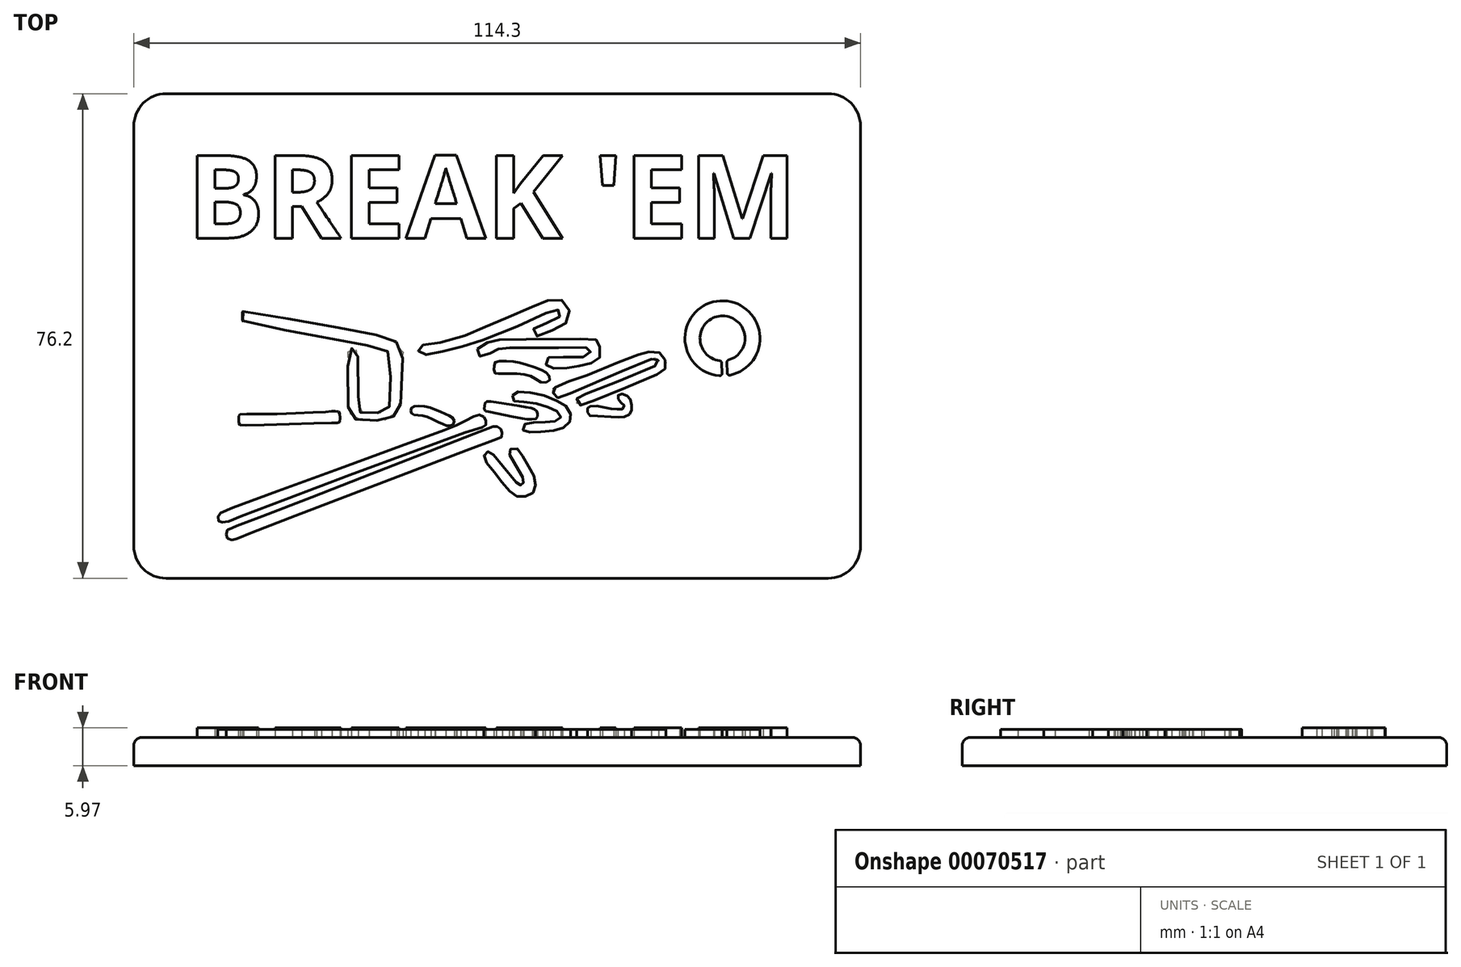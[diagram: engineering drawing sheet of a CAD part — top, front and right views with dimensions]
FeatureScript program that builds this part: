
annotation { "Feature Type Name" : "Feature", "Feature Type Description" : "" }
export const myFeature = defineFeature(function(context is Context, id is Id, definition is map)
    precondition{}
    {
        {
            var Q0;
            Q0=qCreatedBy(makeId("Top.planeOp"),FACE);
            var sketch = newSketch(context, id + "F0", { "sketchPlane" : qUnion([Q0])});
            skLineSegment(sketch, "E0.rect.bottom", {"start": v(57.15, -38.1) * mm, "end": v(-57.15, -38.1) * mm});
            skLineSegment(sketch, "E0.rect.top", {"start": v(57.15, 38.1) * mm, "end": v(-57.15, 38.1) * mm});
            skLineSegment(sketch, "E0.rect.left", {"start": v(57.15, -38.1) * mm, "end": v(57.15, 38.1) * mm});
            skLineSegment(sketch, "E0.rect.right", {"start": v(-57.15, -38.1) * mm, "end": v(-57.15, 38.1) * mm});
            skPoint(sketch, "E0.rect.middle", {"position": v(0, 0) * mm});
            skSolve(sketch);
        }
        {
            var Q0;
            Q0=makeQuery(id+"F0.imprint","IMPRINT",FACE,{"disambiguationData":[TD([[makeQuery(id+"F0.imprint","IMPRINT",EDGE,{"derivedFrom":sQuery(id+"F0.wireOp",EDGE,"E0.rect.bottom")}),-1.0]])]});
            extrude(context, id + "F1", {"entities" : qUnion([Q0]), "depth" : 4.44 * mm});
        }
        {
            var Q0;
            Q0=makeQuery(id+"F1.opExtrude","SWEPT_EDGE",EDGE,{"disambiguationData":[OSD([sQuery(id+"F0.wireOp",EDGE,"E0.rect.bottom"),sQuery(id+"F0.wireOp",EDGE,"E0.rect.right")])]});
            var Q1;
            Q1=makeQuery(id+"F1.opExtrude","SWEPT_EDGE",EDGE,{"disambiguationData":[OSD([sQuery(id+"F0.wireOp",EDGE,"E0.rect.bottom"),sQuery(id+"F0.wireOp",EDGE,"E0.rect.left")])]});
            var Q2;
            Q2=makeQuery(id+"F1.opExtrude","SWEPT_EDGE",EDGE,{"disambiguationData":[OSD([sQuery(id+"F0.wireOp",EDGE,"E0.rect.top"),sQuery(id+"F0.wireOp",EDGE,"E0.rect.left")])]});
            var Q3;
            Q3=makeQuery(id+"F1.opExtrude","SWEPT_EDGE",EDGE,{"disambiguationData":[OSD([sQuery(id+"F0.wireOp",EDGE,"E0.rect.top"),sQuery(id+"F0.wireOp",EDGE,"E0.rect.right")])]});
            fillet(context, id + "F2", {"entities" : qUnion([Q0, Q1, Q2, Q3]), "radius" : 5.08 * mm, "tangentPropagation" : true, "allowEdgeOverflow" : false});
        }
        {
            var Q0;
            Q0=makeQuery(id+"F1.opExtrude","CAP_FACE",FACE,{"disambiguationData":[OSD([sQuery(id+"F0.wireOp",EDGE,"E0.rect.bottom"),sQuery(id+"F0.wireOp",EDGE,"E0.rect.top"),sQuery(id+"F0.wireOp",EDGE,"E0.rect.left"),sQuery(id+"F0.wireOp",EDGE,"E0.rect.right")])],"isStart":false});
            var sketch = newSketch(context, id + "F3", { "sketchPlane" : qUnion([Q0])});
            skFitSpline(sketch, "E1", {"points": [v(-39.94, 3.87) * mm, v(-33.53, 2.82) * mm, v(-25.08, 1.33) * mm, v(-19.72, 0.36) * mm, v(-17.93, -0.18) * mm, v(-16.53, -0.66) * mm, v(-15.41, -1.2) * mm, v(-14.9, -2.03) * mm, v(-14.83, -3.42) * mm, v(-15.17, -10.42) * mm, v(-15.45, -11.43) * mm, v(-15.7, -11.97) * mm, v(-16.18, -12.48) * mm, v(-16.68, -12.87) * mm, v(-17.47, -13.16) * mm, v(-18.32, -13.24) * mm, v(-21.28, -13.3) * mm, v(-21.78, -13.26) * mm, v(-22.24, -13.1) * mm, v(-22.71, -12.74) * mm, v(-23.2, -12.06) * mm, v(-23.4, -11.35) * mm, v(-23.45, -10.11) * mm, v(-23.49, -2.72) * mm, v(-23.36, -2.2) * mm, v(-23.16, -2) * mm, v(-22.9, -1.92) * mm, v(-22.58, -1.92) * mm, v(-22.22, -2.08) * mm, v(-22, -2.47) * mm, v(-21.88, -3.16) * mm, v(-21.87, -3.78) * mm, v(-21.86, -10.73) * mm, v(-21.86, -11.38) * mm, v(-21.83, -11.74) * mm, v(-21.67, -11.92) * mm, v(-21.4, -12.02) * mm, v(-20.92, -12.08) * mm, v(-19.89, -12.1) * mm, v(-18.2, -11.99) * mm, v(-17.61, -11.82) * mm, v(-17.24, -11.5) * mm, v(-17.03, -11.24) * mm, v(-16.87, -10.9) * mm, v(-16.82, -10.46) * mm, v(-16.73, -4.34) * mm, v(-16.76, -2.95) * mm, v(-17.52, -2.23) * mm, v(-19.01, -1.77) * mm, v(-20.47, -1.44) * mm, v(-39.51, 2.08) * mm, v(-39.86, 2.2) * mm, v(-40.02, 2.41) * mm, v(-40.07, 2.7) * mm, v(-40.08, 3.14) * mm, v(-40.07, 3.59) * mm, v(-40.08, 3.74) * mm, v(-39.94, 3.87) * mm]});
            skFitSpline(sketch, "E2", {"points": [v(-40.45, -12.34) * mm, v(-35.1, -12.26) * mm, v(-26.4, -11.88) * mm, v(-25.87, -11.83) * mm, v(-25.43, -11.81) * mm, v(-24.97, -11.87) * mm, v(-24.79, -12) * mm, v(-24.73, -12.4) * mm, v(-24.7, -13.25) * mm, v(-24.82, -13.57) * mm, v(-25.04, -13.64) * mm, v(-25.77, -13.64) * mm, v(-40.22, -14.04) * mm, v(-40.46, -13.97) * mm, v(-40.63, -13.75) * mm, v(-40.68, -13.43) * mm, v(-40.66, -12.95) * mm, v(-40.63, -12.57) * mm, v(-40.55, -12.4) * mm, v(-40.45, -12.34) * mm]});
            skFitSpline(sketch, "E3", {"points": [v(-11.7, -1.39) * mm, v(-10.41, -1.25) * mm, v(-8.79, -1) * mm, v(-5.92, -0.22) * mm, v(-2.9, 1) * mm, v(-1.54, 1.55) * mm, v(0.23, 2.29) * mm, v(3.91, 3.93) * mm, v(6.4, 4.95) * mm, v(7.52, 5.42) * mm, v(8.38, 5.68) * mm, v(9.24, 5.82) * mm, v(10.27, 5.62) * mm, v(10.95, 4.99) * mm, v(11.28, 4.27) * mm, v(11.46, 3.38) * mm, v(11.28, 2.5) * mm, v(10.57, 1.83) * mm, v(9.66, 1.32) * mm, v(8.5, 0.82) * mm, v(7.2, 0.26) * mm, v(6.24, -0.02) * mm, v(5.74, 0) * mm, v(5.58, 0.23) * mm, v(5.63, 1) * mm, v(6.3, 1.44) * mm, v(7.15, 1.79) * mm, v(8.1, 2.16) * mm, v(8.97, 2.54) * mm, v(9.92, 3.1) * mm, v(10.12, 3.62) * mm, v(10.07, 3.83) * mm, v(9.91, 4.02) * mm, v(9.43, 4.14) * mm, v(8.77, 4.06) * mm, v(7.9, 3.72) * mm, v(6.85, 3.2) * mm, v(-0.6, -0.07) * mm, v(-3.24, -0.93) * mm, v(-5.46, -1.67) * mm, v(-7.64, -2.23) * mm, v(-8.97, -2.53) * mm, v(-10.44, -2.83) * mm, v(-11.46, -2.96) * mm, v(-12.11, -2.9) * mm, v(-12.34, -2.72) * mm, v(-12.4, -2.39) * mm, v(-12.43, -2) * mm, v(-12.32, -1.66) * mm, v(-12.1, -1.5) * mm, v(-11.7, -1.39) * mm]});
            skFitSpline(sketch, "E4", {"points": [v(-3.13, -2.04) * mm, v(-2.66, -1.65) * mm, v(-1.66, -1.1) * mm, v(-0.8, -0.79) * mm, v(0.3, -0.58) * mm, v(1.42, -0.53) * mm, v(14.73, -0.43) * mm, v(15.24, -0.5) * mm, v(15.63, -0.63) * mm, v(15.95, -0.88) * mm, v(16.1, -1.27) * mm, v(16.16, -1.63) * mm, v(16.2, -2.68) * mm, v(16.16, -3.25) * mm, v(15.87, -3.69) * mm, v(15.3, -4.03) * mm, v(14.5, -4.36) * mm, v(13.53, -4.62) * mm, v(12.66, -4.77) * mm, v(11.78, -4.9) * mm, v(10.65, -5.05) * mm, v(9.4, -5.1) * mm, v(8.65, -5.1) * mm, v(8.08, -4.9) * mm, v(7.76, -4.64) * mm, v(7.6, -4.22) * mm, v(7.63, -3.73) * mm, v(7.95, -3.45) * mm, v(8.6, -3.35) * mm, v(10.44, -3.34) * mm, v(13.22, -3.31) * mm, v(13.96, -3.18) * mm, v(14.46, -2.92) * mm, v(14.7, -2.46) * mm, v(14.65, -2.02) * mm, v(14.45, -1.84) * mm, v(14, -1.79) * mm, v(13.2, -1.81) * mm, v(1.34, -1.84) * mm, v(0.86, -1.89) * mm, v(0.41, -2) * mm, v(-0.26, -2.3) * mm, v(-0.72, -2.53) * mm, v(-1.17, -2.79) * mm, v(-1.77, -3.16) * mm, v(-2.62, -3.22) * mm, v(-3.01, -2.92) * mm, v(-3.3, -2.45) * mm, v(-3.13, -2.04) * mm]});
            skFitSpline(sketch, "E5", {"points": [v(-0.47, -4.68) * mm, v(-0.44, -4.33) * mm, v(-0.3, -4.09) * mm, v(0.14, -3.97) * mm, v(1.12, -3.94) * mm, v(2.13, -3.99) * mm, v(3.21, -4.1) * mm, v(4.14, -4.35) * mm, v(5.42, -4.75) * mm, v(6.85, -5.3) * mm, v(7.44, -5.6) * mm, v(7.9, -5.93) * mm, v(8.2, -6.34) * mm, v(8.3, -6.7) * mm, v(8.14, -7.1) * mm, v(7.78, -7.29) * mm, v(7.16, -7.35) * mm, v(6.43, -7.02) * mm, v(5.75, -6.56) * mm, v(5.17, -6.26) * mm, v(4.16, -6) * mm, v(3, -5.93) * mm, v(1.95, -5.91) * mm, v(1.07, -5.91) * mm, v(0.44, -5.91) * mm, v(-0.12, -5.94) * mm, v(-0.3, -5.86) * mm, v(-0.4, -5.7) * mm, v(-0.48, -5.4) * mm, v(-0.48, -5.03) * mm, v(-0.47, -4.68) * mm]});
            skFitSpline(sketch, "E6", {"points": [v(9.15, -8.1) * mm, v(10.14, -7.66) * mm, v(11.72, -6.97) * mm, v(13.8, -6.3) * mm, v(19.96, -3.76) * mm, v(22.12, -2.93) * mm, v(23, -2.66) * mm, v(23.67, -2.49) * mm, v(24.41, -2.43) * mm, v(25.1, -2.49) * mm, v(25.63, -2.67) * mm, v(26.1, -3.11) * mm, v(26.34, -3.53) * mm, v(26.5, -4.03) * mm, v(26.54, -4.53) * mm, v(26.44, -5.03) * mm, v(26.22, -5.37) * mm, v(25.8, -5.7) * mm, v(25.03, -6.1) * mm, v(17.26, -9.31) * mm, v(14.07, -10.64) * mm, v(13.36, -10.9) * mm, v(12.67, -10.73) * mm, v(12.51, -10.35) * mm, v(12.5, -9.94) * mm, v(12.78, -9.56) * mm, v(13.49, -9.23) * mm, v(14.86, -8.76) * mm, v(24.7, -4.8) * mm, v(25.24, -4.39) * mm, v(25.36, -4.11) * mm, v(25.35, -3.9) * mm, v(25.24, -3.7) * mm, v(24.92, -3.54) * mm, v(24.63, -3.54) * mm, v(24.31, -3.63) * mm, v(23.7, -3.84) * mm, v(10.5, -9.44) * mm, v(10.03, -9.63) * mm, v(9.66, -9.7) * mm, v(9.35, -9.64) * mm, v(9.03, -9.41) * mm, v(8.88, -9.17) * mm, v(8.82, -8.96) * mm, v(8.78, -8.75) * mm, v(8.82, -8.47) * mm, v(8.91, -8.28) * mm, v(9.15, -8.1) * mm]});
            skFitSpline(sketch, "E7", {"points": [v(14.61, -11.04) * mm, v(15.42, -11) * mm, v(16.72, -11.2) * mm, v(17.68, -11.41) * mm, v(18.18, -11.46) * mm, v(18.93, -11.5) * mm, v(19.43, -11.5) * mm, v(19.91, -11.4) * mm, v(20.02, -11.05) * mm, v(19.83, -10.76) * mm, v(19.54, -10.52) * mm, v(19.2, -10.16) * mm, v(19.05, -9.9) * mm, v(18.98, -9.62) * mm, v(19.03, -9.37) * mm, v(19.18, -9.2) * mm, v(19.57, -9.11) * mm, v(20.04, -9.19) * mm, v(20.63, -9.57) * mm, v(20.86, -9.82) * mm, v(21.08, -10.38) * mm, v(21.13, -11) * mm, v(21.15, -11.45) * mm, v(21.09, -11.91) * mm, v(20.83, -12.31) * mm, v(20.33, -12.6) * mm, v(19.6, -12.78) * mm, v(19.07, -12.79) * mm, v(17.85, -12.7) * mm, v(14.99, -12.52) * mm, v(14.53, -12.51) * mm, v(14.3, -12.31) * mm, v(14.21, -11.87) * mm, v(14.2, -11.63) * mm, v(14.2, -11.35) * mm, v(14.4, -11.11) * mm, v(14.61, -11.04) * mm]});
            skFitSpline(sketch, "E8", {"points": [v(2.4, -9.34) * mm, v(2.6, -8.93) * mm, v(3.01, -8.75) * mm, v(3.71, -8.78) * mm, v(5.1, -8.9) * mm, v(6.83, -9.2) * mm, v(8.28, -9.67) * mm, v(9.6, -10.29) * mm, v(10.44, -10.72) * mm, v(11.1, -11.26) * mm, v(11.46, -11.94) * mm, v(11.55, -12.54) * mm, v(11.57, -13.09) * mm, v(11.43, -13.53) * mm, v(11.08, -14.06) * mm, v(10.36, -14.47) * mm, v(9.63, -14.72) * mm, v(8.52, -14.9) * mm, v(7.1, -15.02) * mm, v(5.81, -15.12) * mm, v(5.14, -15.13) * mm, v(4.52, -15.1) * mm, v(4.16, -14.88) * mm, v(4.05, -14.66) * mm, v(4.05, -14.29) * mm, v(4.24, -13.95) * mm, v(4.64, -13.77) * mm, v(5.3, -13.65) * mm, v(6.26, -13.57) * mm, v(7.47, -13.54) * mm, v(8.31, -13.48) * mm, v(9.1, -13.39) * mm, v(9.74, -13.18) * mm, v(9.95, -12.94) * mm, v(10.01, -12.62) * mm, v(9.9, -12.24) * mm, v(9.48, -11.89) * mm, v(8.95, -11.62) * mm, v(8.05, -11.22) * mm, v(7, -10.82) * mm, v(5.61, -10.5) * mm, v(4.27, -10.4) * mm, v(3.45, -10.34) * mm, v(2.7, -10.26) * mm, v(2.47, -10.06) * mm, v(2.41, -9.8) * mm, v(2.4, -9.34) * mm]});
            skFitSpline(sketch, "E9", {"points": [v(-1.97, -11) * mm, v(-1.94, -10.66) * mm, v(-1.81, -10.38) * mm, v(-1.44, -10.25) * mm, v(-0.66, -10.34) * mm, v(1.55, -10.67) * mm, v(3.9, -11.09) * mm, v(5.26, -11.33) * mm, v(5.82, -11.48) * mm, v(6.2, -11.77) * mm, v(6.3, -12) * mm, v(6.33, -12.26) * mm, v(6.35, -12.51) * mm, v(6.2, -12.96) * mm, v(5.83, -13.08) * mm, v(4.83, -13.07) * mm, v(3.8, -12.94) * mm, v(-1.48, -11.9) * mm, v(-1.79, -11.84) * mm, v(-1.98, -11.63) * mm, v(-2, -11.34) * mm, v(-1.97, -11) * mm]});
            skFitSpline(sketch, "E10", {"points": [v(1.97, -18.7) * mm, v(1.92, -18.15) * mm, v(2.05, -17.81) * mm, v(2.44, -17.65) * mm, v(3, -17.63) * mm, v(3.5, -18.02) * mm, v(4.1, -19.07) * mm, v(4.9, -20.43) * mm, v(5.6, -21.59) * mm, v(5.95, -22.63) * mm, v(6.04, -23.54) * mm, v(5.85, -24.33) * mm, v(5.32, -24.93) * mm, v(4.56, -25.23) * mm, v(3.69, -25.29) * mm, v(2.95, -25.14) * mm, v(2.24, -24.7) * mm, v(1.43, -23.8) * mm, v(0.26, -22.36) * mm, v(-0.79, -20.98) * mm, v(-1.75, -19.81) * mm, v(-2.06, -19.12) * mm, v(-2, -18.64) * mm, v(-1.83, -18.36) * mm, v(-1.53, -18.2) * mm, v(-1.17, -18.18) * mm, v(-0.72, -18.53) * mm, v(0.1, -19.52) * mm, v(3.03, -23.04) * mm, v(3.34, -23.36) * mm, v(3.53, -23.44) * mm, v(3.8, -23.44) * mm, v(3.98, -23.36) * mm, v(4.1, -23.23) * mm, v(4.16, -22.97) * mm, v(4.14, -22.65) * mm, v(4.05, -22.27) * mm, v(3.87, -21.92) * mm, v(3.6, -21.48) * mm, v(1.97, -18.7) * mm]});
            skFitSpline(sketch, "E11", {"points": [v(-13.58, -11.73) * mm, v(-13.58, -11.48) * mm, v(-13.35, -11.18) * mm, v(-12.93, -11.02) * mm, v(-12.22, -11) * mm, v(-11.01, -11.1) * mm, v(-10.08, -11.42) * mm, v(-9.09, -11.81) * mm, v(-8.1, -12.27) * mm, v(-7.6, -12.5) * mm, v(-7.1, -12.77) * mm, v(-6.78, -13.21) * mm, v(-6.8, -13.67) * mm, v(-7, -13.99) * mm, v(-7.32, -14.1) * mm, v(-7.77, -14.1) * mm, v(-8.3, -13.97) * mm, v(-9.03, -13.63) * mm, v(-10.17, -13.07) * mm, v(-11.19, -12.64) * mm, v(-12, -12.51) * mm, v(-12.62, -12.44) * mm, v(-13.15, -12.34) * mm, v(-13.44, -12.16) * mm, v(-13.58, -11.93) * mm, v(-13.58, -11.73) * mm]});
            skFitSpline(sketch, "E12", {"points": [v(-2.1, -12.68) * mm, v(-2.34, -12.48) * mm, v(-2.7, -12.38) * mm, v(-3.26, -12.43) * mm, v(-3.73, -12.64) * mm, v(-4.85, -13.25) * mm, v(-6.32, -13.98) * mm, v(-7.44, -14.48) * mm, v(-43.27, -27.67) * mm, v(-43.5, -27.81) * mm, v(-43.73, -28.01) * mm, v(-43.85, -28.2) * mm, v(-43.93, -28.5) * mm, v(-43.95, -28.86) * mm, v(-43.82, -29.1) * mm, v(-43.6, -29.25) * mm, v(-43.37, -29.28) * mm, v(-42.94, -29.3) * mm, v(-42.29, -29.15) * mm, v(-41.47, -28.82) * mm, v(-2.64, -14.41) * mm, v(-2.29, -14.36) * mm, v(-1.98, -14.2) * mm, v(-1.8, -14.01) * mm, v(-1.77, -13.75) * mm, v(-1.77, -13.46) * mm, v(-1.85, -13.1) * mm, v(-1.9, -12.92) * mm, v(-2.1, -12.68) * mm]});
            skFitSpline(sketch, "E13", {"points": [v(0.56, -14.64) * mm, v(0.36, -14.41) * mm, v(0, -14.24) * mm, v(-0.43, -14.2) * mm, v(-1.08, -14.41) * mm, v(-40.98, -29.88) * mm, v(-41.36, -30.02) * mm, v(-41.9, -30.22) * mm, v(-42.36, -30.42) * mm, v(-42.53, -30.78) * mm, v(-42.6, -31.17) * mm, v(-42.53, -31.52) * mm, v(-42.4, -31.82) * mm, v(-42.17, -31.97) * mm, v(-41.69, -32.05) * mm, v(-41.14, -31.96) * mm, v(-40.39, -31.64) * mm, v(0.33, -16.04) * mm, v(0.55, -15.97) * mm, v(0.74, -15.83) * mm, v(0.82, -15.5) * mm, v(0.78, -15.16) * mm, v(0.7, -14.9) * mm, v(0.56, -14.64) * mm]});
            skArc(sketch, "E14", {"start": v(36.62, -6.15) * mm, "mid": v(35.09, 5.53) * mm, "end": v(34.95, -6.25) * mm});
            skArc(sketch, "E15", {"start": v(36.4, -3.77) * mm, "mid": v(35.18, 3.16) * mm, "end": v(35, -3.87) * mm});
            skLineSegment(sketch, "E16", {"start": v(35.33, -4.24) * mm, "end": v(35.37, -5.86) * mm});
            skLineSegment(sketch, "E17", {"start": v(36.13, -4.14) * mm, "end": v(36.17, -5.79) * mm});
            skPoint(sketch, "E18.visualSharp", {"position": v(35.32, -3.9) * mm});
            skArc(sketch, "E18.filletArc", {"start": v(35.33, -4.24) * mm, "mid": v(35.23, -4) * mm, "end": v(35, -3.87) * mm});
            skPoint(sketch, "E19.visualSharp", {"position": v(35.38, -6.27) * mm});
            skArc(sketch, "E19.filletArc", {"start": v(34.95, -6.25) * mm, "mid": v(35.25, -6.15) * mm, "end": v(35.37, -5.86) * mm});
            skPoint(sketch, "E20.visualSharp", {"position": v(36.12, -3.83) * mm});
            skArc(sketch, "E20.filletArc", {"start": v(36.4, -3.77) * mm, "mid": v(36.2, -3.9) * mm, "end": v(36.13, -4.14) * mm});
            skPoint(sketch, "E21.visualSharp", {"position": v(36.18, -6.22) * mm});
            skArc(sketch, "E21.filletArc", {"start": v(36.17, -5.79) * mm, "mid": v(36.3, -6.07) * mm, "end": v(36.62, -6.15) * mm});
            skSolve(sketch);
        }
        {
            var Q0;
            Q0 = qSketchRegion(id + "F3", true);
            extrude(context, id + "F4", {"entities" : qUnion([Q0]), "operationType" : NewBodyOperationType.ADD, "depth" : 1.27 * mm});
        }
        {
            var Q0;
            Q0=makeQuery(id+"F1.opExtrude","CAP_FACE",FACE,{"disambiguationData":[OSD([sQuery(id+"F0.wireOp",EDGE,"E0.rect.bottom"),sQuery(id+"F0.wireOp",EDGE,"E0.rect.top"),sQuery(id+"F0.wireOp",EDGE,"E0.rect.left"),sQuery(id+"F0.wireOp",EDGE,"E0.rect.right")])],"isStart":false});
            var sketch = newSketch(context, id + "F5", { "sketchPlane" : qUnion([Q0])});
            skText(sketch, "E22", { "text": "BREAK \'EM", "fontName": "OpenSans-Bold.ttf"});
            const initialGuessF5  = {"E22": [-0.0488, 0.01539, 1, 0, 0.01311]};
            skSetInitialGuess(sketch, initialGuessF5);
            skSolve(sketch);
        }
        {
            var Q0;
            Q0 = qSketchRegion(id + "F5", true);
            extrude(context, id + "F6", {"entities" : qUnion([Q0]), "operationType" : NewBodyOperationType.ADD, "depth" : 1.52 * mm});
        }
        {
            var Q0;
            Q0=makeQuery(id+"F1.opExtrude","CAP_EDGE",EDGE,{"disambiguationData":[OSD([sQuery(id+"F0.wireOp",EDGE,"E0.rect.top")])],"isStart":false});
            fillet(context, id + "F7", {"entities" : qUnion([Q0]), "radius" : 1.27 * mm, "tangentPropagation" : true, "allowEdgeOverflow" : false});
        }
    });
